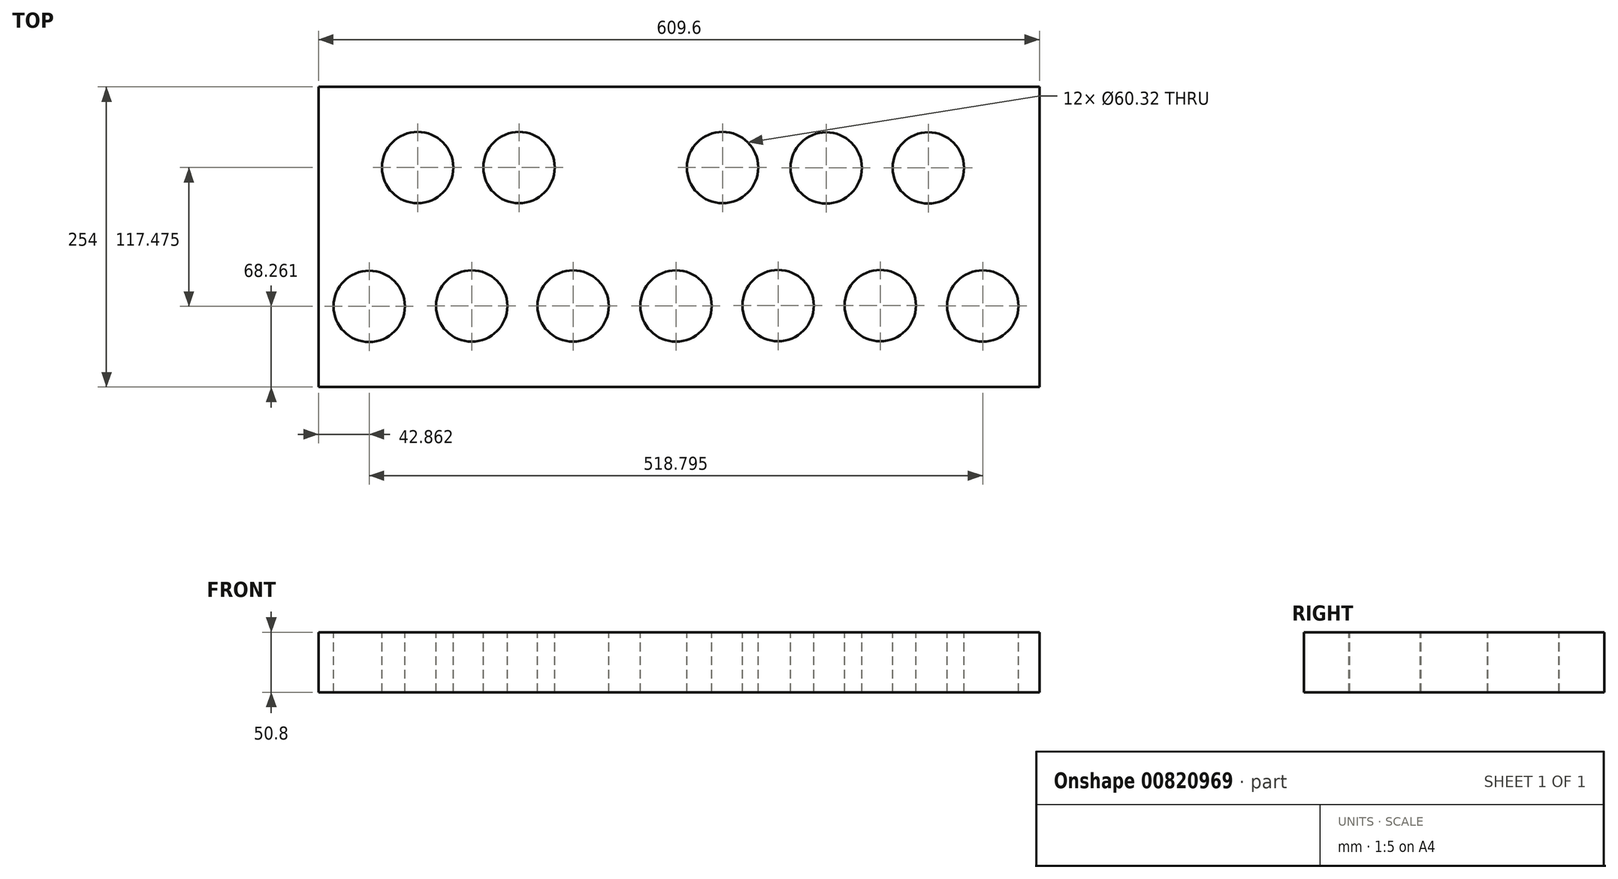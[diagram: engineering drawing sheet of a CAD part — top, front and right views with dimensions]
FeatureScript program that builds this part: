
annotation { "Feature Type Name" : "Feature", "Feature Type Description" : "" }
export const myFeature = defineFeature(function(context is Context, id is Id, definition is map)
    precondition{}
    {
        {
            var Q0;
            Q0=qCreatedBy(makeId("Right.planeOp"),FACE);
            var sketch = newSketch(context, id + "F0", { "sketchPlane" : qUnion([Q0])});
            skLineSegment(sketch, "E0.bottom", {"start": v(-137.62, 0) * mm, "end": v(116.38, 0) * mm});
            skLineSegment(sketch, "E0.top", {"start": v(-137.62, -50.8) * mm, "end": v(116.38, -50.8) * mm});
            skLineSegment(sketch, "E0.left", {"start": v(-137.62, 0) * mm, "end": v(-137.62, -50.8) * mm});
            skLineSegment(sketch, "E0.right", {"start": v(116.38, 0) * mm, "end": v(116.38, -50.8) * mm});
            skSolve(sketch);
        }
        {
            var Q0;
            Q0=makeQuery(id+"F0.imprint","IMPRINT",FACE,{"disambiguationData":[TD([[makeQuery(id+"F0.imprint","IMPRINT",EDGE,{"derivedFrom":sQuery(id+"F0.wireOp",EDGE,"E0.bottom")}),-1.0]])]});
            extrude(context, id + "F1", {"entities" : qUnion([Q0]), "depth" : 609.6 * mm, "offsetDistance" : 25.4 * mm});
        }
        {
            var Q0;
            Q0=qCreatedBy(makeId("Top.planeOp"),FACE);
            var sketch = newSketch(context, id + "F2", { "sketchPlane" : qUnion([Q0])});
            skCircle(sketch, "E1", {"center": v(42.86, -69.36) * mm, "radius": 30.16 * mm});
            skCircle(sketch, "E2", {"center": v(83.82, 48.12) * mm, "radius": 30.16 * mm});
            skCircle(sketch, "E3", {"center": v(129.54, -69.04) * mm, "radius": 30.16 * mm});
            skCircle(sketch, "E4", {"center": v(169.54, 48.12) * mm, "radius": 30.16 * mm});
            skCircle(sketch, "E5", {"center": v(215.27, -69.04) * mm, "radius": 30.16 * mm});
            skCircle(sketch, "E6", {"center": v(302.26, -69.04) * mm, "radius": 30.16 * mm});
            skCircle(sketch, "E7", {"center": v(388.63, -68.72) * mm, "radius": 30.16 * mm});
            skCircle(sketch, "E8", {"center": v(341.63, 48.12) * mm, "radius": 30.16 * mm});
            skCircle(sketch, "E9", {"center": v(429.26, 47.8) * mm, "radius": 30.16 * mm});
            skCircle(sketch, "E10", {"center": v(515.62, 47.8) * mm, "radius": 30.16 * mm});
            skCircle(sketch, "E11", {"center": v(474.98, -68.72) * mm, "radius": 30.16 * mm});
            skCircle(sketch, "E12", {"center": v(561.66, -69.04) * mm, "radius": 30.16 * mm});
            skPoint(sketch, "E13", {"position": v(0, 0) * mm});
            skPoint(sketch, "E14", {"position": v(267.9, -194.18) * mm});
            skLineSegment(sketch, "E15", {"start": v(388.63, -38.56) * mm, "end": v(474.98, -38.56) * mm});
            skLineSegment(sketch, "E16", {"start": v(609.6, -146.49) * mm, "end": v(609.6, 129.23) * mm});
            skSolve(sketch);
        }
        {
            var Q0;
            Q0 = qSketchRegion(id + "F2", true);
            extrude(context, id + "F3", {"entities" : qUnion([Q0]), "operationType" : NewBodyOperationType.REMOVE, "oppositeDirection" : true, "depth" : 107.2 * mm, "offsetDistance" : 25.4 * mm});
        }
    });
